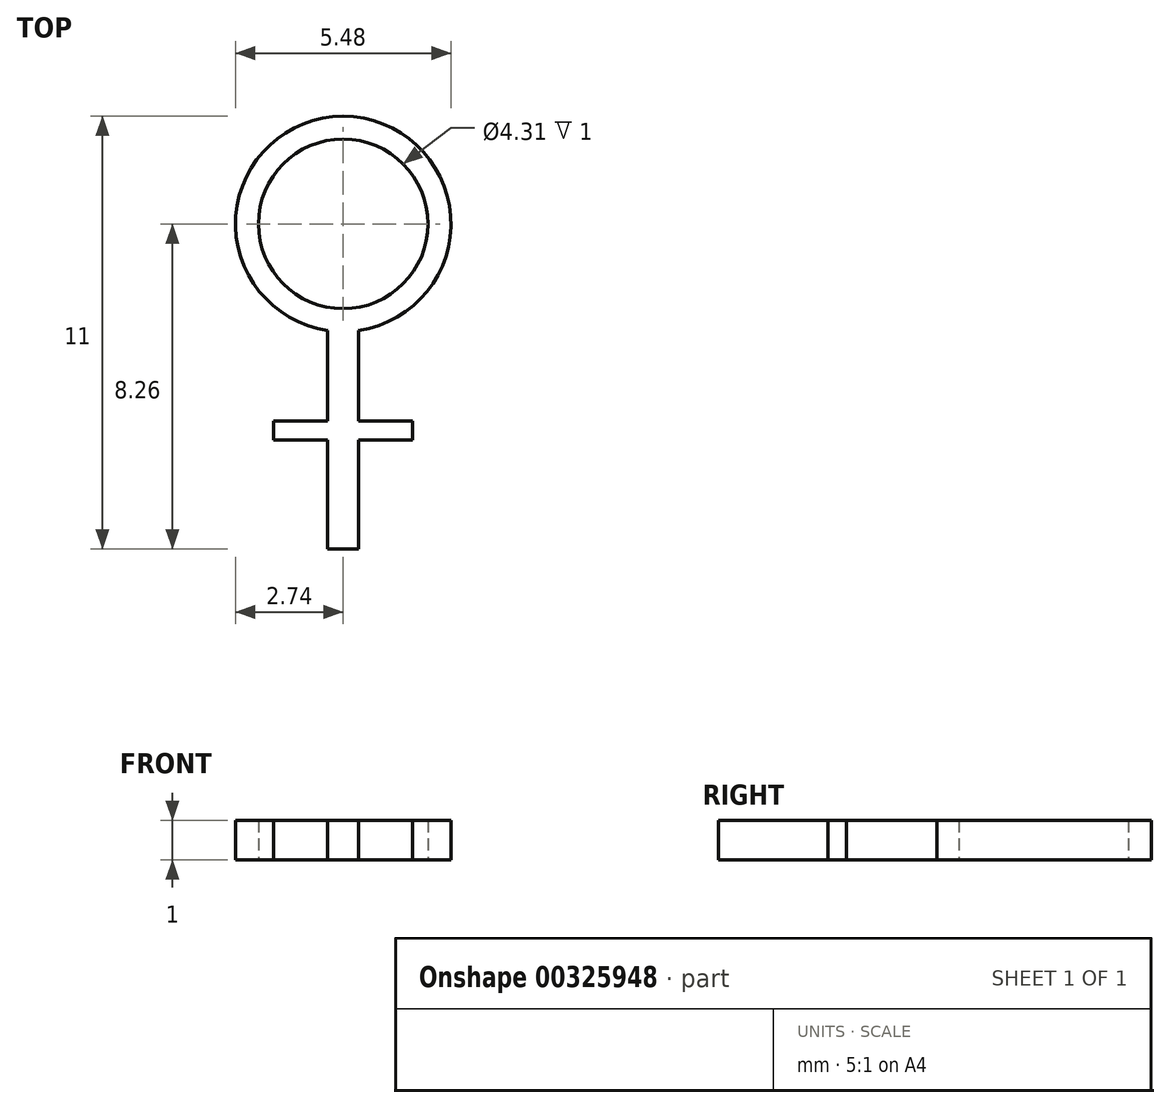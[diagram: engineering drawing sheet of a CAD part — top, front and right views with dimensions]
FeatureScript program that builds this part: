
annotation { "Feature Type Name" : "Feature", "Feature Type Description" : "" }
export const myFeature = defineFeature(function(context is Context, id is Id, definition is map)
    precondition{}
    {
        {
            var Q0;
            Q0=qCreatedBy(makeId("Top.planeOp"),FACE);
            var sketch = newSketch(context, id + "F0", { "sketchPlane" : qUnion([Q0])});
            skArc(sketch, "E0", {"start": v(0.4, -2.7) * mm, "mid": v(0, 2.74) * mm, "end": v(-0.4, -2.7) * mm});
            skCircle(sketch, "E1", {"center": v(0, 0) * mm, "radius": 2.15 * mm});
            skLineSegment(sketch, "E2", {"start": v(-0.4, -5.49) * mm, "end": v(-0.4, -8.26) * mm});
            skLineSegment(sketch, "E3", {"start": v(0.4, -5.49) * mm, "end": v(0.4, -8.26) * mm});
            skLineSegment(sketch, "E4", {"start": v(-0.4, -8.26) * mm, "end": v(0.4, -8.26) * mm});
            skPoint(sketch, "E5.orphan", {"position": v(0, -8.26) * mm});
            skPoint(sketch, "E6.start.orphan", {"position": v(0, 2.74) * mm});
            skPoint(sketch, "E7.oppositeSnap0", {"position": v(0.4, -5.49) * mm});
            skPoint(sketch, "E7.right.end.orphan", {"position": v(2.4, -5.49) * mm});
            skLineSegment(sketch, "E8", {"start": v(-0.4, -2.7) * mm, "end": v(-0.4, -5.01) * mm});
            skLineSegment(sketch, "E9", {"start": v(-0.4, -5.01) * mm, "end": v(-1.77, -5.01) * mm});
            skLineSegment(sketch, "E10", {"start": v(-1.77, -5.01) * mm, "end": v(-1.77, -5.49) * mm});
            skLineSegment(sketch, "E11", {"start": v(-1.77, -5.49) * mm, "end": v(-0.4, -5.49) * mm});
            skLineSegment(sketch, "E12", {"start": v(0.4, -2.7) * mm, "end": v(0.4, -5.01) * mm});
            skLineSegment(sketch, "E13", {"start": v(0.4, -5.01) * mm, "end": v(1.77, -5.01) * mm});
            skLineSegment(sketch, "E14", {"start": v(1.77, -5.01) * mm, "end": v(1.77, -5.49) * mm});
            skLineSegment(sketch, "E15", {"start": v(1.77, -5.49) * mm, "end": v(0.4, -5.49) * mm});
            skSolve(sketch);
        }
        {
            var Q0;
            Q0=makeQuery(id+"F0.imprint","IMPRINT",FACE,{"disambiguationData":[TD([[makeQuery(id+"F0.imprint","IMPRINT",EDGE,{"derivedFrom":sQuery(id+"F0.wireOp",EDGE,"E0")}),1.0]])]});
            extrude(context, id + "F1", {"entities" : qUnion([Q0]), "depth" : 1 * mm});
        }
    });
